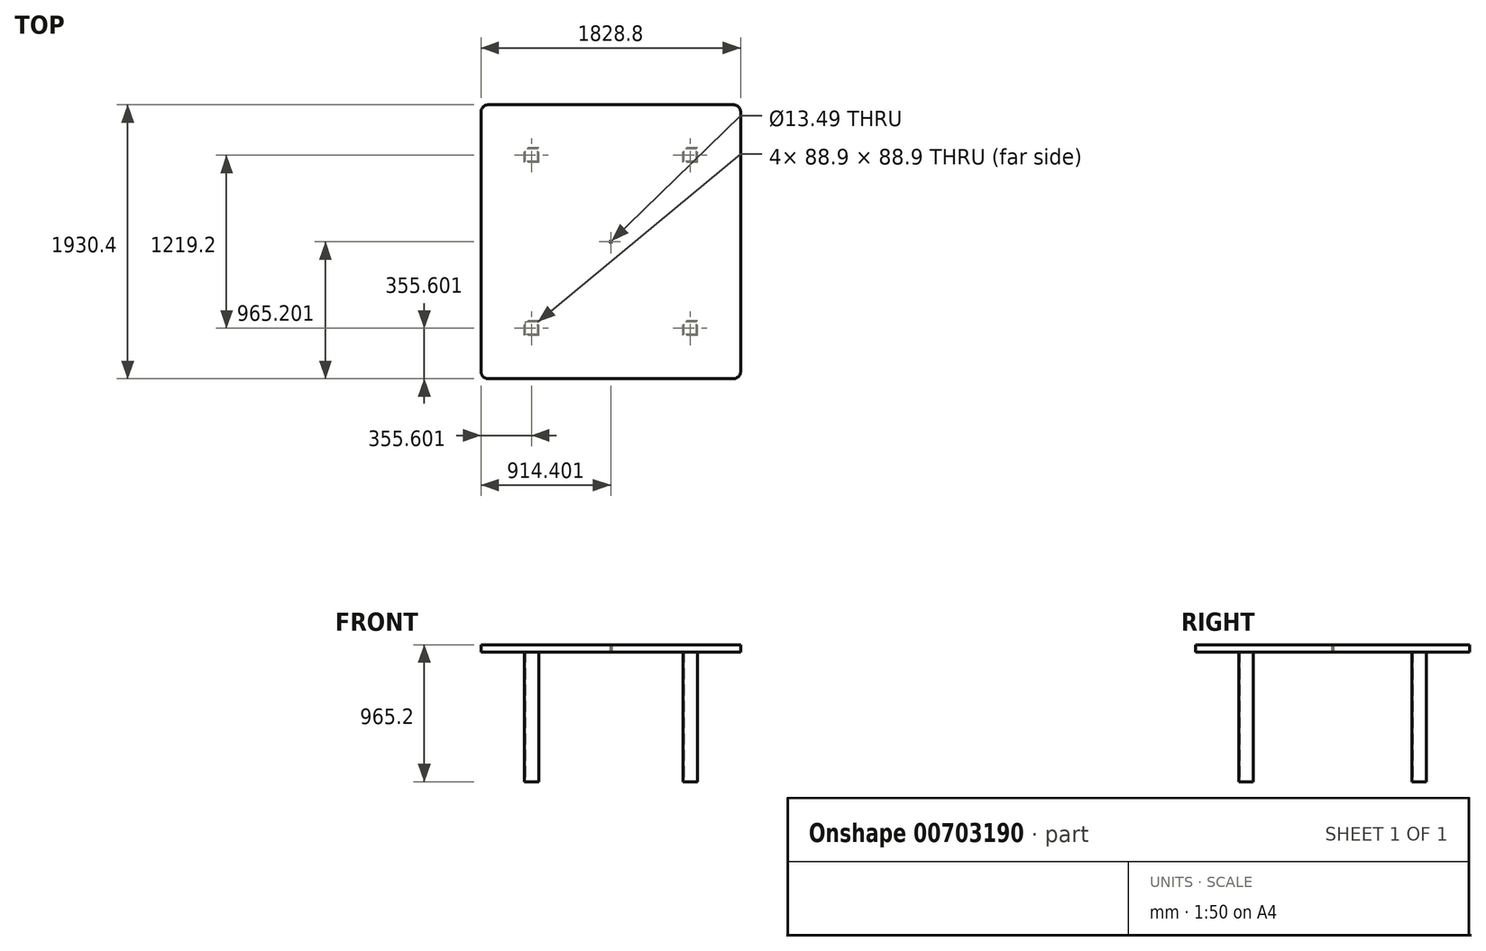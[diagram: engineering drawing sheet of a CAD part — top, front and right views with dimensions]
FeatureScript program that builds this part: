
annotation { "Feature Type Name" : "Feature", "Feature Type Description" : "" }
export const myFeature = defineFeature(function(context is Context, id is Id, definition is map)
    precondition{}
    {
        {
            var Q0;
            Q0=qCreatedBy(makeId("Top.planeOp"),FACE);
            var sketch = newSketch(context, id + "F0", { "sketchPlane" : qUnion([Q0])});
            skLineSegment(sketch, "E0.bottom", {"start": v(-219.97, 166.26) * mm, "end": v(-321.57, 166.26) * mm});
            skLineSegment(sketch, "E0.top", {"start": v(-219.97, 267.86) * mm, "end": v(-321.57, 267.86) * mm});
            skLineSegment(sketch, "E0.left", {"start": v(-219.97, 166.26) * mm, "end": v(-219.97, 267.86) * mm});
            skLineSegment(sketch, "E0.right", {"start": v(-321.57, 166.26) * mm, "end": v(-321.57, 267.86) * mm});
            skPoint(sketch, "E0.middle", {"position": v(-270.77, 217.06) * mm});
            skLineSegment(sketch, "E1.bottom", {"start": v(897.63, 166.26) * mm, "end": v(796.03, 166.26) * mm});
            skLineSegment(sketch, "E1.top", {"start": v(897.63, 267.86) * mm, "end": v(796.03, 267.86) * mm});
            skLineSegment(sketch, "E1.left", {"start": v(897.63, 166.26) * mm, "end": v(897.63, 267.86) * mm});
            skLineSegment(sketch, "E1.right", {"start": v(796.03, 166.26) * mm, "end": v(796.03, 267.86) * mm});
            skPoint(sketch, "E1.middle", {"position": v(846.83, 217.06) * mm});
            skLineSegment(sketch, "E2.bottom", {"start": v(897.63, -1052.94) * mm, "end": v(796.03, -1052.94) * mm});
            skLineSegment(sketch, "E2.top", {"start": v(897.63, -951.34) * mm, "end": v(796.03, -951.34) * mm});
            skLineSegment(sketch, "E2.left", {"start": v(897.63, -1052.94) * mm, "end": v(897.63, -951.34) * mm});
            skLineSegment(sketch, "E2.right", {"start": v(796.03, -1052.94) * mm, "end": v(796.03, -951.34) * mm});
            skPoint(sketch, "E2.middle", {"position": v(846.83, -1002.14) * mm});
            skLineSegment(sketch, "E3.bottom", {"start": v(-219.97, -1052.94) * mm, "end": v(-321.57, -1052.94) * mm});
            skLineSegment(sketch, "E3.top", {"start": v(-219.97, -951.34) * mm, "end": v(-321.57, -951.34) * mm});
            skLineSegment(sketch, "E3.left", {"start": v(-219.97, -1052.94) * mm, "end": v(-219.97, -951.34) * mm});
            skLineSegment(sketch, "E3.right", {"start": v(-321.57, -1052.94) * mm, "end": v(-321.57, -951.34) * mm});
            skPoint(sketch, "E3.middle", {"position": v(-270.77, -1002.14) * mm});
            skLineSegment(sketch, "E4.0", {"start": v(-315.22, 172.61) * mm, "end": v(-315.22, 261.51) * mm});
            skLineSegment(sketch, "E4.1", {"start": v(-226.32, 172.61) * mm, "end": v(-315.22, 172.61) * mm});
            skLineSegment(sketch, "E4.2", {"start": v(-226.32, 172.61) * mm, "end": v(-226.32, 261.51) * mm});
            skLineSegment(sketch, "E4.3", {"start": v(-226.32, 261.51) * mm, "end": v(-315.22, 261.51) * mm});
            skLineSegment(sketch, "E5.0", {"start": v(802.38, 172.61) * mm, "end": v(802.38, 261.51) * mm});
            skLineSegment(sketch, "E5.1", {"start": v(891.28, 172.61) * mm, "end": v(802.38, 172.61) * mm});
            skLineSegment(sketch, "E5.2", {"start": v(891.28, 172.61) * mm, "end": v(891.28, 261.51) * mm});
            skLineSegment(sketch, "E5.3", {"start": v(891.28, 261.51) * mm, "end": v(802.38, 261.51) * mm});
            skLineSegment(sketch, "E6.0", {"start": v(-315.22, -1046.59) * mm, "end": v(-315.22, -957.69) * mm});
            skLineSegment(sketch, "E6.1", {"start": v(-226.32, -1046.59) * mm, "end": v(-315.22, -1046.59) * mm});
            skLineSegment(sketch, "E6.2", {"start": v(-226.32, -1046.59) * mm, "end": v(-226.32, -957.69) * mm});
            skLineSegment(sketch, "E6.3", {"start": v(-226.32, -957.69) * mm, "end": v(-315.22, -957.69) * mm});
            skLineSegment(sketch, "E7.0", {"start": v(802.38, -1046.59) * mm, "end": v(802.38, -957.69) * mm});
            skLineSegment(sketch, "E7.1", {"start": v(891.28, -1046.59) * mm, "end": v(802.38, -1046.59) * mm});
            skLineSegment(sketch, "E7.2", {"start": v(891.28, -1046.59) * mm, "end": v(891.28, -957.69) * mm});
            skLineSegment(sketch, "E7.3", {"start": v(891.28, -957.69) * mm, "end": v(802.38, -957.69) * mm});
            skSolve(sketch);
        }
        {
            var Q0;
            Q0=makeQuery(id+"F0.imprint","IMPRINT",FACE,{"disambiguationData":[TD([[makeQuery(id+"F0.imprint","IMPRINT",EDGE,{"derivedFrom":sQuery(id+"F0.wireOp",EDGE,"E0.bottom")}),-1.0]])]});
            var Q1;
            Q1=makeQuery(id+"F0.imprint","IMPRINT",FACE,{"disambiguationData":[TD([[makeQuery(id+"F0.imprint","IMPRINT",EDGE,{"derivedFrom":sQuery(id+"F0.wireOp",EDGE,"E1.bottom")}),-1.0]])]});
            var Q2;
            Q2=makeQuery(id+"F0.imprint","IMPRINT",FACE,{"disambiguationData":[TD([[makeQuery(id+"F0.imprint","IMPRINT",EDGE,{"derivedFrom":sQuery(id+"F0.wireOp",EDGE,"E3.bottom")}),-1.0]])]});
            var Q3;
            Q3=makeQuery(id+"F0.imprint","IMPRINT",FACE,{"disambiguationData":[TD([[makeQuery(id+"F0.imprint","IMPRINT",EDGE,{"derivedFrom":sQuery(id+"F0.wireOp",EDGE,"E2.bottom")}),-1.0]])]});
            extrude(context, id + "F1", {"entities" : qUnion([Q0, Q1, Q2, Q3]), "depth" : 914.4 * mm, "offsetDistance" : 25.4 * mm});
        }
        {
            var Q0;
            Q0=makeQuery(id+"F1.opExtrude","CAP_FACE",FACE,{"disambiguationData":[OSD([sQuery(id+"F0.wireOp",EDGE,"E3.bottom"),sQuery(id+"F0.wireOp",EDGE,"E3.top"),sQuery(id+"F0.wireOp",EDGE,"E3.left"),sQuery(id+"F0.wireOp",EDGE,"E3.right"),sQuery(id+"F0.wireOp",EDGE,"E6.0"),sQuery(id+"F0.wireOp",EDGE,"E6.1"),sQuery(id+"F0.wireOp",EDGE,"E6.2"),sQuery(id+"F0.wireOp",EDGE,"E6.3")])],"isStart":false});
            var sketch = newSketch(context, id + "F2", { "sketchPlane" : qUnion([Q0])});
            skLineSegment(sketch, "E8.bottom", {"start": v(-626.37, 572.66) * mm, "end": v(1202.43, 572.66) * mm});
            skLineSegment(sketch, "E8.top", {"start": v(-626.37, -1357.74) * mm, "end": v(1202.43, -1357.74) * mm});
            skLineSegment(sketch, "E8.left", {"start": v(-626.37, 572.66) * mm, "end": v(-626.37, -1357.74) * mm});
            skLineSegment(sketch, "E8.right", {"start": v(1202.43, 572.66) * mm, "end": v(1202.43, -1357.74) * mm});
            skPoint(sketch, "E8.middle", {"position": v(288.03, -392.54) * mm});
            skSolve(sketch);
        }
        {
            var Q0;
            Q0 = qSketchRegion(id + "F2", true);
            extrude(context, id + "F3", {"entities" : qUnion([Q0]), "depth" : 50.8 * mm, "offsetDistance" : 25.4 * mm});
        }
        {
            var Q0;
            Q0=makeQuery(id+"F3.opExtrude","SWEPT_EDGE",EDGE,{"disambiguationData":[OSD([sQuery(id+"F2.wireOp",EDGE,"E8.top"),sQuery(id+"F2.wireOp",EDGE,"E8.right")])]});
            var Q1;
            Q1=makeQuery(id+"F3.opExtrude","SWEPT_EDGE",EDGE,{"disambiguationData":[OSD([sQuery(id+"F2.wireOp",EDGE,"E8.bottom"),sQuery(id+"F2.wireOp",EDGE,"E8.right")])]});
            fillet(context, id + "F4", {"entities" : qUnion([Q0, Q1]), "radius" : 50.8 * mm, "tangentPropagation" : true, "allowEdgeOverflow" : false});
        }
        {
            var Q0;
            Q0=makeQuery(id+"F3.opExtrude","SWEPT_EDGE",EDGE,{"disambiguationData":[OSD([sQuery(id+"F2.wireOp",EDGE,"E8.bottom"),sQuery(id+"F2.wireOp",EDGE,"E8.left")])]});
            var Q1;
            Q1=makeQuery(id+"F3.opExtrude","SWEPT_EDGE",EDGE,{"disambiguationData":[OSD([sQuery(id+"F2.wireOp",EDGE,"E8.top"),sQuery(id+"F2.wireOp",EDGE,"E8.left")])]});
            fillet(context, id + "F5", {"entities" : qUnion([Q0, Q1]), "radius" : 50.8 * mm, "tangentPropagation" : true, "allowEdgeOverflow" : false});
        }
        {
            var Q0;
            Q0=sQuery(id+"F2.wireOp",VERTEX,"E8.middle");
            var Q1;
            Q1=makeQuery(id+"F3.opExtrude","SWEPT_BODY",BODY,{"disambiguationData":[OSD([sQuery(id+"F2.wireOp",EDGE,"E8.bottom"),sQuery(id+"F2.wireOp",EDGE,"E8.top"),sQuery(id+"F2.wireOp",EDGE,"E8.left"),sQuery(id+"F2.wireOp",EDGE,"E8.right")])]});
            hole(context, id + "F6", {"style" : HoleStyle.SIMPLE, "endStyle" : HoleEndStyle.THROUGH, "oppositeDirection" : true, "standardTappedOrClearance" : lookupTablePath({ "standard" : "ANSI", "fit" : "Normal (ASME)", "size" : "1/2", "type" : "Clearance" }), "standardBlindInLast" : lookupTablePath({ "fit" : "Free", "standard" : "ANSI", "size" : "1/2", "type" : "Clearance" }), "holeDiameter" : 13.5 * mm, "majorDiameter" : 6.35 * mm, "isTappedThrough" : true, "tappedDepth" : 12.7 * mm, "tapClearance" : 3, "locations" : qUnion([Q0]), "scope" : qUnion([Q1])});
        }
    });
